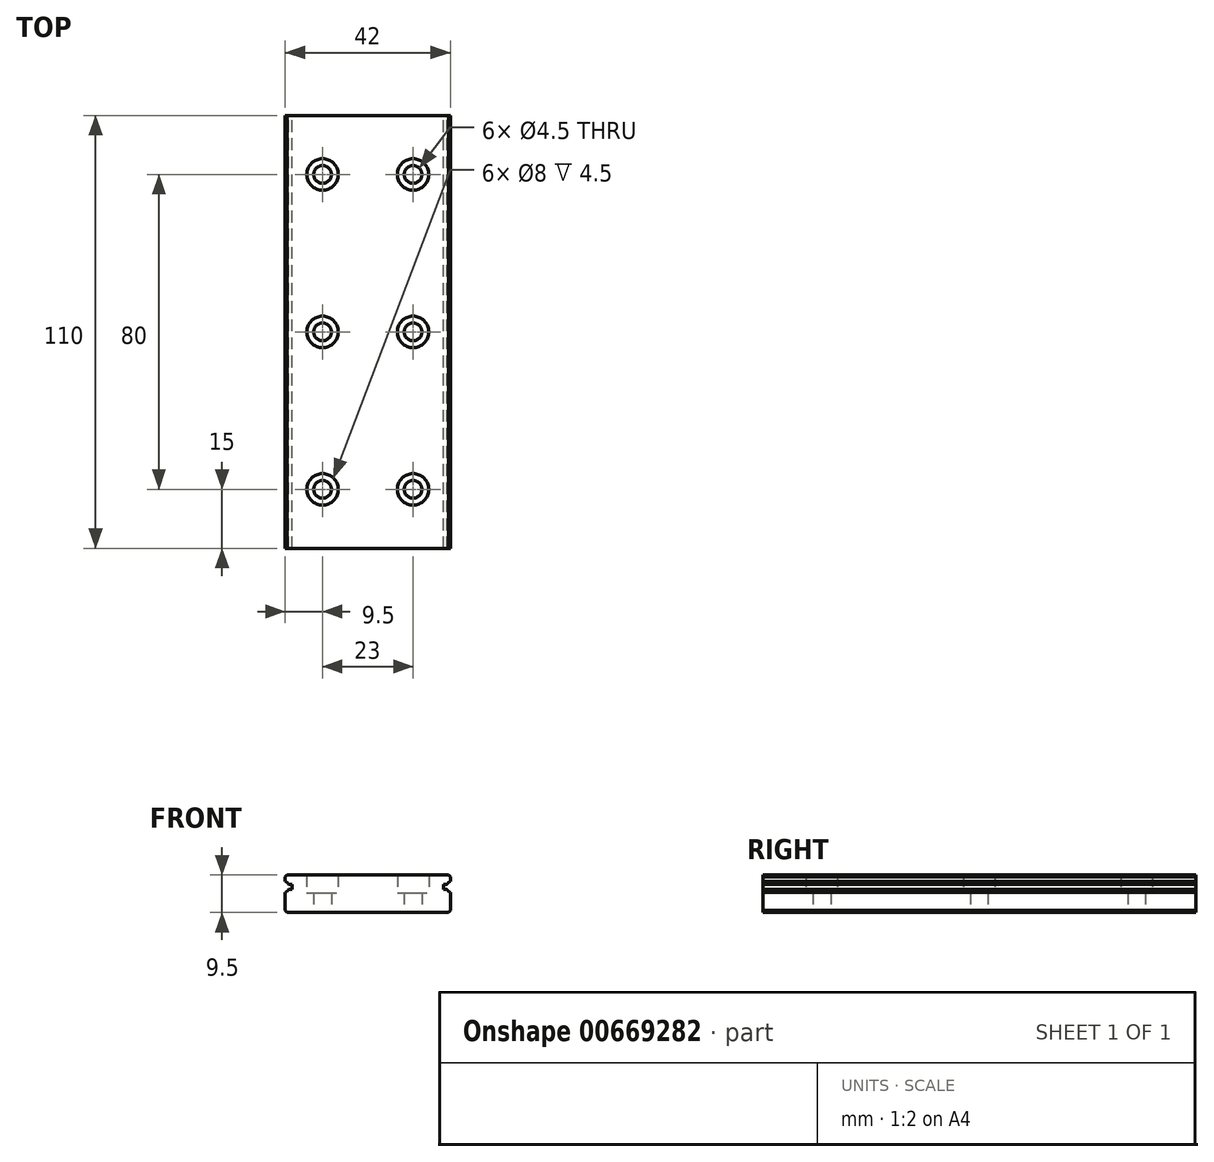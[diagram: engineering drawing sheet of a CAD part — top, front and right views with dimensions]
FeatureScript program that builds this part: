
annotation { "Feature Type Name" : "Feature", "Feature Type Description" : "" }
export const myFeature = defineFeature(function(context is Context, id is Id, definition is map)
    precondition{}
    {
        {
            assignVariable(context, id + "F0", {"variableType" : VariableType.LENGTH, "name" : "D", "lengthValue" : 8 * mm});
        }
        {
            assignVariable(context, id + "F1", {"variableType" : VariableType.LENGTH, "name" : "d", "lengthValue" : 4.5 * mm});
        }
        {
            assignVariable(context, id + "F2", {"variableType" : VariableType.LENGTH, "name" : "h", "lengthValue" : 4.5 * mm});
        }
        {
            var Q0;
            Q0=qCreatedBy(makeId("Front.planeOp"),FACE);
            var sketch = newSketch(context, id + "F3", { "sketchPlane" : qUnion([Q0])});
            skLineSegment(sketch, "E0.bottom", {"start": v(0, -4.75) * mm, "end": v(-20.5, -4.75) * mm});
            skLineSegment(sketch, "E0.right", {"start": v(-21, -4.26) * mm, "end": v(-21, 0.34) * mm});
            skArc(sketch, "E1", {"start": v(-21, 0.34) * mm, "mid": v(-20.48, 0.65) * mm, "end": v(-20.13, 1.15) * mm});
            skLineSegment(sketch, "E2", {"start": v(-19.2, 1.15) * mm, "end": v(-20.13, 1.15) * mm});
            skLineSegment(sketch, "E3", {"start": v(-19.2, 2.35) * mm, "end": v(-20.13, 2.35) * mm});
            skLineSegment(sketch, "E4", {"start": v(-21, 4.26) * mm, "end": v(-20.5, 4.75) * mm});
            skLineSegment(sketch, "E5.MirrorCS", {"start": v(-21, -4.26) * mm, "end": v(-20.5, -4.75) * mm});
            skPoint(sketch, "E6.orphan", {"position": v(-21, 4.75) * mm});
            skLineSegment(sketch, "E7.trimOffspring", {"start": v(-21, 3.16) * mm, "end": v(-21, 4.26) * mm});
            skArc(sketch, "E8.trimOffspring", {"start": v(-20.13, 2.35) * mm, "mid": v(-20.48, 2.85) * mm, "end": v(-21, 3.16) * mm});
            skPoint(sketch, "E9.orphan", {"position": v(-21, -4.75) * mm});
            skLineSegment(sketch, "E10", {"start": v(-20.5, 4.75) * mm, "end": v(0, 4.75) * mm});
            skLineSegment(sketch, "E11", {"start": v(-19.2, 2.35) * mm, "end": v(-19.2, 1.15) * mm});
            skLineSegment(sketch, "E12", {"start": v(-21.5, 1.75) * mm, "end": v(0, 1.75) * mm, "construction": true});
            skLineSegment(sketch, "E13.MirrorCS", {"start": v(21, 4.26) * mm, "end": v(20.5, 4.75) * mm});
            skLineSegment(sketch, "E14.MirrorCS", {"start": v(21, -4.26) * mm, "end": v(20.5, -4.75) * mm});
            skLineSegment(sketch, "E15.MirrorCS", {"start": v(19.2, 2.35) * mm, "end": v(19.2, 1.15) * mm});
            skLineSegment(sketch, "E16.MirrorCS", {"start": v(21, 3.16) * mm, "end": v(21, 4.26) * mm});
            skPoint(sketch, "E17.MirrorP", {"position": v(21, 4.75) * mm});
            skPoint(sketch, "E18.MirrorP", {"position": v(21, -4.75) * mm});
            skLineSegment(sketch, "E19.MirrorCS", {"start": v(21, -4.26) * mm, "end": v(21, 0.34) * mm});
            skArc(sketch, "E20.MirrorCS", {"start": v(21, 0.34) * mm, "mid": v(20.48, 0.65) * mm, "end": v(20.13, 1.15) * mm});
            skLineSegment(sketch, "E21.MirrorCS", {"start": v(19.2, 1.15) * mm, "end": v(20.13, 1.15) * mm});
            skLineSegment(sketch, "E22.MirrorCS", {"start": v(19.2, 2.35) * mm, "end": v(20.13, 2.35) * mm});
            skArc(sketch, "E23.MirrorCS", {"start": v(20.13, 2.35) * mm, "mid": v(20.48, 2.85) * mm, "end": v(21, 3.16) * mm});
            skLineSegment(sketch, "E24.MirrorCS", {"start": v(20.5, 4.75) * mm, "end": v(0, 4.75) * mm});
            skLineSegment(sketch, "E25.MirrorCS", {"start": v(0, -4.75) * mm, "end": v(20.5, -4.75) * mm});
            skSolve(sketch);
        }
        {
            var Q0;
            Q0=makeQuery(id+"F3.imprint","IMPRINT",FACE,{"disambiguationData":[TD([[makeQuery(id+"F3.imprint","IMPRINT",EDGE,{"derivedFrom":sQuery(id+"F3.wireOp",EDGE,"E0.bottom")}),-1.0]])]});
            extrude(context, id + "F4", {"entities" : qUnion([Q0]), "depth" : 110 * mm, "offsetDistance" : 25 * mm});
        }
        {
            var Q0;
            Q0=makeQuery(id+"F4.opExtrude","SWEPT_FACE",FACE,{"disambiguationData":[OSD([sQuery(id+"F3.wireOp",EDGE,"E10"),sQuery(id+"F3.wireOp",EDGE,"E24.MirrorCS")])]});
            var sketch = newSketch(context, id + "F5", { "sketchPlane" : qUnion([Q0])});
            skPoint(sketch, "E26", {"position": v(-11.5, -15) * mm});
            skPoint(sketch, "E27", {"position": v(11.5, -15) * mm});
            skPoint(sketch, "E28.0.1.0", {"position": v(-11.5, -55) * mm});
            skPoint(sketch, "E28.0.1.1", {"position": v(11.5, -55) * mm});
            skPoint(sketch, "E28.0.2.0", {"position": v(-11.5, -95) * mm});
            skPoint(sketch, "E28.0.2.1", {"position": v(11.5, -95) * mm});
            skPoint(sketch, "E28.0.3.0", {"position": v(-11.5, -135) * mm});
            skPoint(sketch, "E28.0.3.1", {"position": v(11.5, -135) * mm});
            skPoint(sketch, "E28.0.4.0", {"position": v(-11.5, -175) * mm});
            skPoint(sketch, "E28.0.4.1", {"position": v(11.5, -175) * mm});
            skPoint(sketch, "E28.0.5.0", {"position": v(-11.5, -215) * mm});
            skPoint(sketch, "E28.0.5.1", {"position": v(11.5, -215) * mm});
            skPoint(sketch, "E28.0.6.0", {"position": v(-11.5, -255) * mm});
            skPoint(sketch, "E28.0.6.1", {"position": v(11.5, -255) * mm});
            skPoint(sketch, "E28.0.7.0", {"position": v(-11.5, -295) * mm});
            skPoint(sketch, "E28.0.7.1", {"position": v(11.5, -295) * mm});
            skPoint(sketch, "E28.0.8.0", {"position": v(-11.5, -335) * mm});
            skPoint(sketch, "E28.0.8.1", {"position": v(11.5, -335) * mm});
            skPoint(sketch, "E28.0.9.0", {"position": v(-11.5, -375) * mm});
            skPoint(sketch, "E28.0.9.1", {"position": v(11.5, -375) * mm});
            skPoint(sketch, "E28.0.10.0", {"position": v(-11.5, -415) * mm});
            skPoint(sketch, "E28.0.10.1", {"position": v(11.5, -415) * mm});
            skPoint(sketch, "E28.0.11.0", {"position": v(-11.5, -455) * mm});
            skPoint(sketch, "E28.0.11.1", {"position": v(11.5, -455) * mm});
            skPoint(sketch, "E28.0.12.0", {"position": v(-11.5, -495) * mm});
            skPoint(sketch, "E28.0.12.1", {"position": v(11.5, -495) * mm});
            skPoint(sketch, "E28.0.13.0", {"position": v(-11.5, -535) * mm});
            skPoint(sketch, "E28.0.13.1", {"position": v(11.5, -535) * mm});
            skPoint(sketch, "E28.0.14.0", {"position": v(-11.5, -575) * mm});
            skPoint(sketch, "E28.0.14.1", {"position": v(11.5, -575) * mm});
            skPoint(sketch, "E28.0.15.0", {"position": v(-11.5, -615) * mm});
            skPoint(sketch, "E28.0.15.1", {"position": v(11.5, -615) * mm});
            skPoint(sketch, "E28.0.16.0", {"position": v(-11.5, -655) * mm});
            skPoint(sketch, "E28.0.16.1", {"position": v(11.5, -655) * mm});
            skPoint(sketch, "E28.0.17.0", {"position": v(-11.5, -695) * mm});
            skPoint(sketch, "E28.0.17.1", {"position": v(11.5, -695) * mm});
            skPoint(sketch, "E28.0.18.0", {"position": v(-11.5, -735) * mm});
            skPoint(sketch, "E28.0.18.1", {"position": v(11.5, -735) * mm});
            skPoint(sketch, "E28.0.19.0", {"position": v(-11.5, -775) * mm});
            skPoint(sketch, "E28.0.19.1", {"position": v(11.5, -775) * mm});
            skPoint(sketch, "E28.0.20.0", {"position": v(-11.5, -815) * mm});
            skPoint(sketch, "E28.0.20.1", {"position": v(11.5, -815) * mm});
            skPoint(sketch, "E28.0.21.0", {"position": v(-11.5, -855) * mm});
            skPoint(sketch, "E28.0.21.1", {"position": v(11.5, -855) * mm});
            skPoint(sketch, "E28.0.22.0", {"position": v(-11.5, -895) * mm});
            skPoint(sketch, "E28.0.22.1", {"position": v(11.5, -895) * mm});
            skPoint(sketch, "E28.0.23.0", {"position": v(-11.5, -935) * mm});
            skPoint(sketch, "E28.0.23.1", {"position": v(11.5, -935) * mm});
            skPoint(sketch, "E28.0.24.0", {"position": v(-11.5, -975) * mm});
            skPoint(sketch, "E28.0.24.1", {"position": v(11.5, -975) * mm});
            skPoint(sketch, "E28.0.25.0", {"position": v(-11.5, -1015) * mm});
            skPoint(sketch, "E28.0.25.1", {"position": v(11.5, -1015) * mm});
            skPoint(sketch, "E28.0.26.0", {"position": v(-11.5, -1055) * mm});
            skPoint(sketch, "E28.0.26.1", {"position": v(11.5, -1055) * mm});
            skPoint(sketch, "E28.0.27.0", {"position": v(-11.5, -1095) * mm});
            skPoint(sketch, "E28.0.27.1", {"position": v(11.5, -1095) * mm});
            skPoint(sketch, "E28.0.28.0", {"position": v(-11.5, -1135) * mm});
            skPoint(sketch, "E28.0.28.1", {"position": v(11.5, -1135) * mm});
            skPoint(sketch, "E28.0.29.0", {"position": v(-11.5, -1175) * mm});
            skPoint(sketch, "E28.0.29.1", {"position": v(11.5, -1175) * mm});
            skPoint(sketch, "E28.0.30.0", {"position": v(-11.5, -1215) * mm});
            skPoint(sketch, "E28.0.30.1", {"position": v(11.5, -1215) * mm});
            skPoint(sketch, "E28.0.31.0", {"position": v(-11.5, -1255) * mm});
            skPoint(sketch, "E28.0.31.1", {"position": v(11.5, -1255) * mm});
            skPoint(sketch, "E28.0.32.0", {"position": v(-11.5, -1295) * mm});
            skPoint(sketch, "E28.0.32.1", {"position": v(11.5, -1295) * mm});
            skPoint(sketch, "E28.0.33.0", {"position": v(-11.5, -1335) * mm});
            skPoint(sketch, "E28.0.33.1", {"position": v(11.5, -1335) * mm});
            skPoint(sketch, "E28.0.34.0", {"position": v(-11.5, -1375) * mm});
            skPoint(sketch, "E28.0.34.1", {"position": v(11.5, -1375) * mm});
            skPoint(sketch, "E28.0.35.0", {"position": v(-11.5, -1415) * mm});
            skPoint(sketch, "E28.0.35.1", {"position": v(11.5, -1415) * mm});
            skPoint(sketch, "E28.0.36.0", {"position": v(-11.5, -1455) * mm});
            skPoint(sketch, "E28.0.36.1", {"position": v(11.5, -1455) * mm});
            skPoint(sketch, "E28.0.37.0", {"position": v(-11.5, -1495) * mm});
            skPoint(sketch, "E28.0.37.1", {"position": v(11.5, -1495) * mm});
            skPoint(sketch, "E28.0.38.0", {"position": v(-11.5, -1535) * mm});
            skPoint(sketch, "E28.0.38.1", {"position": v(11.5, -1535) * mm});
            skPoint(sketch, "E28.0.39.0", {"position": v(-11.5, -1575) * mm});
            skPoint(sketch, "E28.0.39.1", {"position": v(11.5, -1575) * mm});
            skPoint(sketch, "E28.0.40.0", {"position": v(-11.5, -1615) * mm});
            skPoint(sketch, "E28.0.40.1", {"position": v(11.5, -1615) * mm});
            skPoint(sketch, "E28.0.41.0", {"position": v(-11.5, -1655) * mm});
            skPoint(sketch, "E28.0.41.1", {"position": v(11.5, -1655) * mm});
            skPoint(sketch, "E28.0.42.0", {"position": v(-11.5, -1695) * mm});
            skPoint(sketch, "E28.0.42.1", {"position": v(11.5, -1695) * mm});
            skPoint(sketch, "E28.0.43.0", {"position": v(-11.5, -1735) * mm});
            skPoint(sketch, "E28.0.43.1", {"position": v(11.5, -1735) * mm});
            skPoint(sketch, "E28.0.44.0", {"position": v(-11.5, -1775) * mm});
            skPoint(sketch, "E28.0.44.1", {"position": v(11.5, -1775) * mm});
            skPoint(sketch, "E28.0.45.0", {"position": v(-11.5, -1815) * mm});
            skPoint(sketch, "E28.0.45.1", {"position": v(11.5, -1815) * mm});
            skPoint(sketch, "E28.0.46.0", {"position": v(-11.5, -1855) * mm});
            skPoint(sketch, "E28.0.46.1", {"position": v(11.5, -1855) * mm});
            skPoint(sketch, "E28.0.47.0", {"position": v(-11.5, -1895) * mm});
            skPoint(sketch, "E28.0.47.1", {"position": v(11.5, -1895) * mm});
            skPoint(sketch, "E28.0.48.0", {"position": v(-11.5, -1935) * mm});
            skPoint(sketch, "E28.0.48.1", {"position": v(11.5, -1935) * mm});
            skPoint(sketch, "E28.0.49.0", {"position": v(-11.5, -1975) * mm});
            skPoint(sketch, "E28.0.49.1", {"position": v(11.5, -1975) * mm});
            skLineSegment(sketch, "E28.direction1", {"start": v(-11.5, -15) * mm, "end": v(11.5, -15) * mm, "construction": true});
            skLineSegment(sketch, "E28.direction2", {"start": v(-11.5, -15) * mm, "end": v(-11.5, -55) * mm, "construction": true});
            skSolve(sketch);
        }
        {
            var Q0;
            Q0=sQuery(id+"F5.wireOp",VERTEX,"E28.0.16.0");
            var Q1;
            Q1=sQuery(id+"F5.wireOp",VERTEX,"E28.0.8.0");
            var Q2;
            Q2=sQuery(id+"F5.wireOp",VERTEX,"E28.0.11.0");
            var Q3;
            Q3=sQuery(id+"F5.wireOp",VERTEX,"E28.0.19.0");
            var Q4;
            Q4=sQuery(id+"F5.wireOp",VERTEX,"E28.0.15.0");
            var Q5;
            Q5=sQuery(id+"F5.wireOp",VERTEX,"E28.0.7.0");
            var Q6;
            Q6=sQuery(id+"F5.wireOp",VERTEX,"E28.0.10.0");
            var Q7;
            Q7=sQuery(id+"F5.wireOp",VERTEX,"E28.0.18.0");
            var Q8;
            Q8=sQuery(id+"F5.wireOp",VERTEX,"E28.0.14.0");
            var Q9;
            Q9=sQuery(id+"F5.wireOp",VERTEX,"E28.0.9.0");
            var Q10;
            Q10=sQuery(id+"F5.wireOp",VERTEX,"E28.0.6.0");
            var Q11;
            Q11=sQuery(id+"F5.wireOp",VERTEX,"E28.0.5.0");
            var Q12;
            Q12=sQuery(id+"F5.wireOp",VERTEX,"E28.0.13.0");
            var Q13;
            Q13=sQuery(id+"F5.wireOp",VERTEX,"E28.direction2.end");
            var Q14;
            Q14=sQuery(id+"F5.wireOp",VERTEX,"E28.direction2.start");
            var Q15;
            Q15=sQuery(id+"F5.wireOp",VERTEX,"E28.0.4.0");
            var Q16;
            Q16=sQuery(id+"F5.wireOp",VERTEX,"E28.0.17.0");
            var Q17;
            Q17=sQuery(id+"F5.wireOp",VERTEX,"E28.0.2.0");
            var Q18;
            Q18=sQuery(id+"F5.wireOp",VERTEX,"E28.0.3.0");
            var Q19;
            Q19=sQuery(id+"F5.wireOp",VERTEX,"E28.0.12.0");
            var Q20;
            Q20=sQuery(id+"F5.wireOp",VERTEX,"E28.0.11.1");
            var Q21;
            Q21=sQuery(id+"F5.wireOp",VERTEX,"E28.0.19.1");
            var Q22;
            Q22=sQuery(id+"F5.wireOp",VERTEX,"E28.0.15.1");
            var Q23;
            Q23=sQuery(id+"F5.wireOp",VERTEX,"E28.0.7.1");
            var Q24;
            Q24=sQuery(id+"F5.wireOp",VERTEX,"E28.0.10.1");
            var Q25;
            Q25=sQuery(id+"F5.wireOp",VERTEX,"E28.0.18.1");
            var Q26;
            Q26=sQuery(id+"F5.wireOp",VERTEX,"E28.0.17.1");
            var Q27;
            Q27=sQuery(id+"F5.wireOp",VERTEX,"E28.0.3.1");
            var Q28;
            Q28=sQuery(id+"F5.wireOp",VERTEX,"E28.0.9.1");
            var Q29;
            Q29=sQuery(id+"F5.wireOp",VERTEX,"E28.0.5.1");
            var Q30;
            Q30=sQuery(id+"F5.wireOp",VERTEX,"E28.0.6.1");
            var Q31;
            Q31=sQuery(id+"F5.wireOp",VERTEX,"E28.0.12.1");
            var Q32;
            Q32=sQuery(id+"F5.wireOp",VERTEX,"E28.0.4.1");
            var Q33;
            Q33=sQuery(id+"F5.wireOp",VERTEX,"E28.0.2.1");
            var Q34;
            Q34=sQuery(id+"F5.wireOp",VERTEX,"E28.0.1.1");
            var Q35;
            Q35=sQuery(id+"F5.wireOp",VERTEX,"E28.0.13.1");
            var Q36;
            Q36=sQuery(id+"F5.wireOp",VERTEX,"E27");
            var Q37;
            Q37=sQuery(id+"F5.wireOp",VERTEX,"E28.0.14.1");
            var Q38;
            Q38=sQuery(id+"F5.wireOp",VERTEX,"E28.0.16.1");
            var Q39;
            Q39=sQuery(id+"F5.wireOp",VERTEX,"E28.0.8.1");
            var Q40;
            Q40=sQuery(id+"F5.wireOp",VERTEX,"E28.0.35.1");
            var Q41;
            Q41=sQuery(id+"F5.wireOp",VERTEX,"E28.0.43.1");
            var Q42;
            Q42=sQuery(id+"F5.wireOp",VERTEX,"E28.0.27.1");
            var Q43;
            Q43=sQuery(id+"F5.wireOp",VERTEX,"E28.0.48.0");
            var Q44;
            Q44=sQuery(id+"F5.wireOp",VERTEX,"E28.0.24.0");
            var Q45;
            Q45=sQuery(id+"F5.wireOp",VERTEX,"E28.0.32.0");
            var Q46;
            Q46=sQuery(id+"F5.wireOp",VERTEX,"E28.0.40.0");
            var Q47;
            Q47=sQuery(id+"F5.wireOp",VERTEX,"E28.0.35.0");
            var Q48;
            Q48=sQuery(id+"F5.wireOp",VERTEX,"E28.0.43.0");
            var Q49;
            Q49=sQuery(id+"F5.wireOp",VERTEX,"E28.0.27.0");
            var Q50;
            Q50=sQuery(id+"F5.wireOp",VERTEX,"E28.0.47.1");
            var Q51;
            Q51=sQuery(id+"F5.wireOp",VERTEX,"E28.0.23.1");
            var Q52;
            Q52=sQuery(id+"F5.wireOp",VERTEX,"E28.0.31.1");
            var Q53;
            Q53=sQuery(id+"F5.wireOp",VERTEX,"E28.0.39.1");
            var Q54;
            Q54=sQuery(id+"F5.wireOp",VERTEX,"E28.0.34.1");
            var Q55;
            Q55=sQuery(id+"F5.wireOp",VERTEX,"E28.0.42.1");
            var Q56;
            Q56=sQuery(id+"F5.wireOp",VERTEX,"E28.0.26.1");
            var Q57;
            Q57=sQuery(id+"F5.wireOp",VERTEX,"E28.0.47.0");
            var Q58;
            Q58=sQuery(id+"F5.wireOp",VERTEX,"E28.0.23.0");
            var Q59;
            Q59=sQuery(id+"F5.wireOp",VERTEX,"E28.0.31.0");
            var Q60;
            Q60=sQuery(id+"F5.wireOp",VERTEX,"E28.0.39.0");
            var Q61;
            Q61=sQuery(id+"F5.wireOp",VERTEX,"E28.0.34.0");
            var Q62;
            Q62=sQuery(id+"F5.wireOp",VERTEX,"E28.0.42.0");
            var Q63;
            Q63=sQuery(id+"F5.wireOp",VERTEX,"E28.0.26.0");
            var Q64;
            Q64=sQuery(id+"F5.wireOp",VERTEX,"E28.0.46.0");
            var Q65;
            Q65=sQuery(id+"F5.wireOp",VERTEX,"E28.0.49.1");
            var Q66;
            Q66=sQuery(id+"F5.wireOp",VERTEX,"E28.0.25.1");
            var Q67;
            Q67=sQuery(id+"F5.wireOp",VERTEX,"E28.0.41.1");
            var Q68;
            Q68=sQuery(id+"F5.wireOp",VERTEX,"E28.0.30.1");
            var Q69;
            Q69=sQuery(id+"F5.wireOp",VERTEX,"E28.0.37.1");
            var Q70;
            Q70=sQuery(id+"F5.wireOp",VERTEX,"E28.0.33.0");
            var Q71;
            Q71=sQuery(id+"F5.wireOp",VERTEX,"E28.0.45.0");
            var Q72;
            Q72=sQuery(id+"F5.wireOp",VERTEX,"E28.0.36.1");
            var Q73;
            Q73=sQuery(id+"F5.wireOp",VERTEX,"E28.0.29.0");
            var Q74;
            Q74=sQuery(id+"F5.wireOp",VERTEX,"E28.0.44.1");
            var Q75;
            Q75=sQuery(id+"F5.wireOp",VERTEX,"E28.0.28.0");
            var Q76;
            Q76=sQuery(id+"F5.wireOp",VERTEX,"E28.0.20.1");
            var Q77;
            Q77=sQuery(id+"F5.wireOp",VERTEX,"E28.0.28.1");
            var Q78;
            Q78=sQuery(id+"F5.wireOp",VERTEX,"E28.0.49.0");
            var Q79;
            Q79=sQuery(id+"F5.wireOp",VERTEX,"E28.0.21.0");
            var Q80;
            Q80=sQuery(id+"F5.wireOp",VERTEX,"E28.0.45.1");
            var Q81;
            Q81=sQuery(id+"F5.wireOp",VERTEX,"E28.0.48.1");
            var Q82;
            Q82=sQuery(id+"F5.wireOp",VERTEX,"E28.0.29.1");
            var Q83;
            Q83=sQuery(id+"F5.wireOp",VERTEX,"E28.0.41.0");
            var Q84;
            Q84=sQuery(id+"F5.wireOp",VERTEX,"E28.0.46.1");
            var Q85;
            Q85=sQuery(id+"F5.wireOp",VERTEX,"E28.0.40.1");
            var Q86;
            Q86=sQuery(id+"F5.wireOp",VERTEX,"E28.0.32.1");
            var Q87;
            Q87=sQuery(id+"F5.wireOp",VERTEX,"E28.0.22.0");
            var Q88;
            Q88=sQuery(id+"F5.wireOp",VERTEX,"E28.0.20.0");
            var Q89;
            Q89=sQuery(id+"F5.wireOp",VERTEX,"E28.0.30.0");
            var Q90;
            Q90=sQuery(id+"F5.wireOp",VERTEX,"E28.0.36.0");
            var Q91;
            Q91=sQuery(id+"F5.wireOp",VERTEX,"E28.0.22.1");
            var Q92;
            Q92=sQuery(id+"F5.wireOp",VERTEX,"E28.0.24.1");
            var Q93;
            Q93=sQuery(id+"F5.wireOp",VERTEX,"E28.0.33.1");
            var Q94;
            Q94=sQuery(id+"F5.wireOp",VERTEX,"E28.0.38.1");
            var Q95;
            Q95=sQuery(id+"F5.wireOp",VERTEX,"E28.0.37.0");
            var Q96;
            Q96=sQuery(id+"F5.wireOp",VERTEX,"E28.0.38.0");
            var Q97;
            Q97=sQuery(id+"F5.wireOp",VERTEX,"E28.0.44.0");
            var Q98;
            Q98=sQuery(id+"F5.wireOp",VERTEX,"E28.0.25.0");
            var Q99;
            Q99=sQuery(id+"F5.wireOp",VERTEX,"E28.0.21.1");
            var Q100;
            Q100=makeQuery(id+"F4.opExtrude","SWEPT_BODY",BODY,{"disambiguationData":[OSD([sQuery(id+"F3.wireOp",EDGE,"E0.bottom"),sQuery(id+"F3.wireOp",EDGE,"E0.right"),sQuery(id+"F3.wireOp",EDGE,"E1"),sQuery(id+"F3.wireOp",EDGE,"E2"),sQuery(id+"F3.wireOp",EDGE,"E3"),sQuery(id+"F3.wireOp",EDGE,"E4"),sQuery(id+"F3.wireOp",EDGE,"E5.MirrorCS"),sQuery(id+"F3.wireOp",EDGE,"E7.trimOffspring"),sQuery(id+"F3.wireOp",EDGE,"E8.trimOffspring"),sQuery(id+"F3.wireOp",EDGE,"E10"),sQuery(id+"F3.wireOp",EDGE,"E11"),sQuery(id+"F3.wireOp",EDGE,"E13.MirrorCS"),sQuery(id+"F3.wireOp",EDGE,"E14.MirrorCS"),sQuery(id+"F3.wireOp",EDGE,"E15.MirrorCS"),sQuery(id+"F3.wireOp",EDGE,"E16.MirrorCS"),sQuery(id+"F3.wireOp",EDGE,"E19.MirrorCS"),sQuery(id+"F3.wireOp",EDGE,"E20.MirrorCS"),sQuery(id+"F3.wireOp",EDGE,"E21.MirrorCS"),sQuery(id+"F3.wireOp",EDGE,"E22.MirrorCS"),sQuery(id+"F3.wireOp",EDGE,"E23.MirrorCS"),sQuery(id+"F3.wireOp",EDGE,"E24.MirrorCS"),sQuery(id+"F3.wireOp",EDGE,"E25.MirrorCS")])]});
            hole(context, id + "F6", {"style" : HoleStyle.C_BORE, "endStyle" : HoleEndStyle.THROUGH, "holeDiameter" : getVariable(context, 'd'), "cBoreDiameter" : getVariable(context, 'D'), "cBoreDepth" : getVariable(context, 'h'), "majorDiameter" : 5 * mm, "isTappedThrough" : true, "tappedDepth" : 1 * mm, "tapClearance" : 3, "locations" : qUnion([Q0, Q1, Q2, Q3, Q4, Q5, Q6, Q7, Q8, Q9, Q10, Q11, Q12, Q13, Q14, Q15, Q16, Q17, Q18, Q19, Q20, Q21, Q22, Q23, Q24, Q25, Q26, Q27, Q28, Q29, Q30, Q31, Q32, Q33, Q34, Q35, Q36, Q37, Q38, Q39, Q40, Q41, Q42, Q43, Q44, Q45, Q46, Q47, Q48, Q49, Q50, Q51, Q52, Q53, Q54, Q55, Q56, Q57, Q58, Q59, Q60, Q61, Q62, Q63, Q64, Q65, Q66, Q67, Q68, Q69, Q70, Q71, Q72, Q73, Q74, Q75, Q76, Q77, Q78, Q79, Q80, Q81, Q82, Q83, Q84, Q85, Q86, Q87, Q88, Q89, Q90, Q91, Q92, Q93, Q94, Q95, Q96, Q97, Q98, Q99]), "scope" : qUnion([Q100]), "startStyle" : HoleStartStyle.PART});
        }
    });
